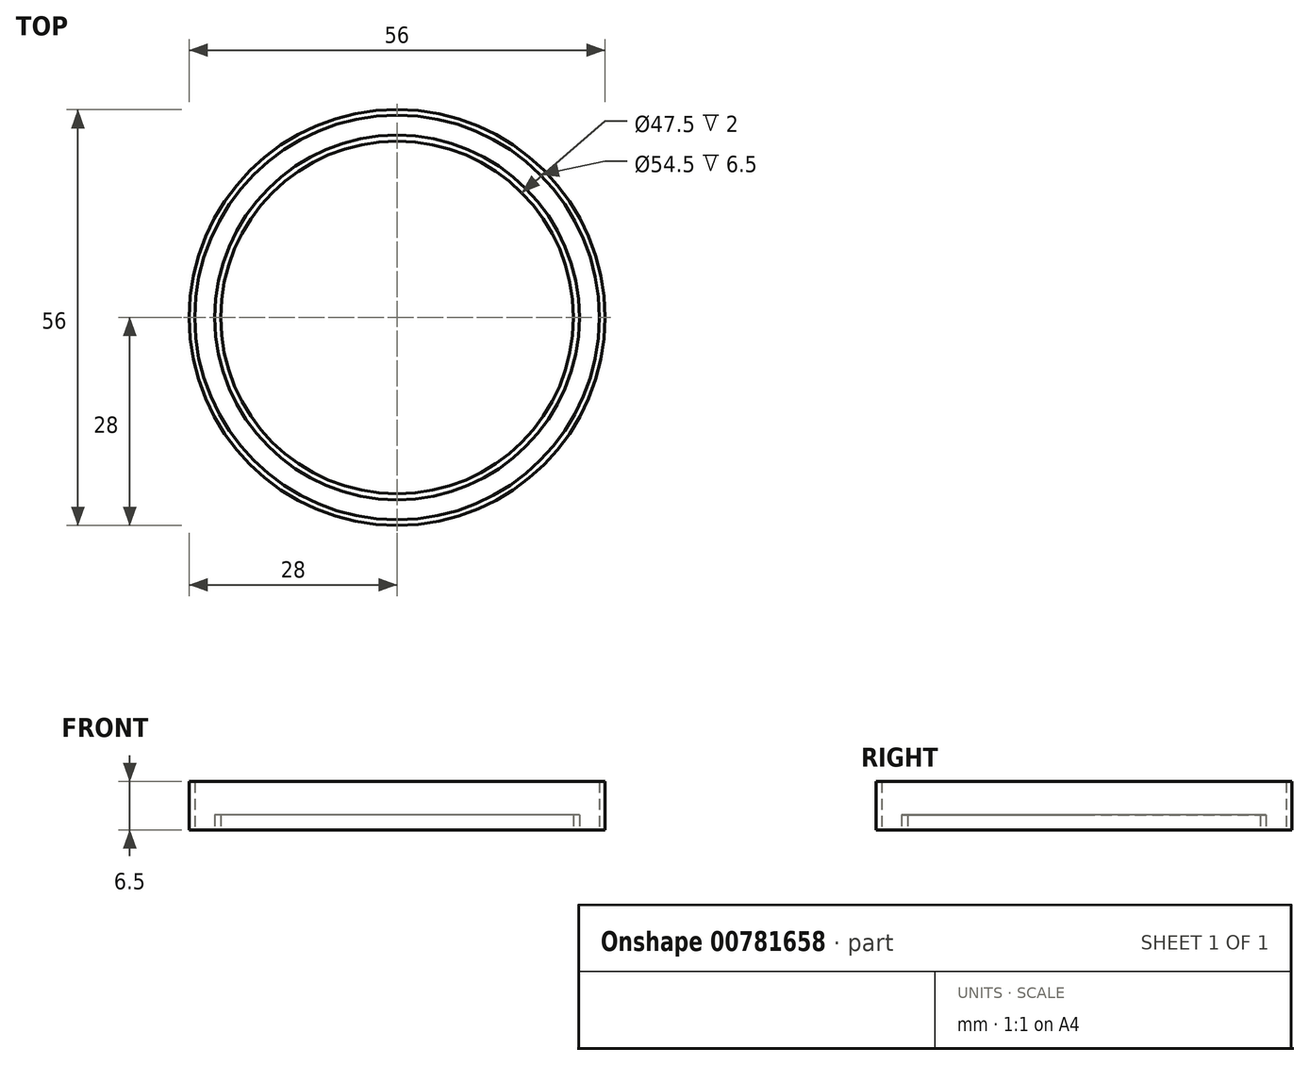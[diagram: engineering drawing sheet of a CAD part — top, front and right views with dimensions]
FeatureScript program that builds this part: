
annotation { "Feature Type Name" : "Feature", "Feature Type Description" : "" }
export const myFeature = defineFeature(function(context is Context, id is Id, definition is map)
    precondition{}
    {
        {
            var Q0;
            Q0=qCreatedBy(makeId("Top.planeOp"),FACE);
            var sketch = newSketch(context, id + "F0", { "sketchPlane" : qUnion([Q0])});
            skCircle(sketch, "E0", {"center": v(0, 0) * mm, "radius": 28 * mm});
            skCircle(sketch, "E1", {"center": v(0, 0) * mm, "radius": 23.75 * mm});
            skCircle(sketch, "E2", {"center": v(0, 0) * mm, "radius": 27.25 * mm});
            skCircle(sketch, "E3", {"center": v(0, 0) * mm, "radius": 24.55 * mm});
            skLineSegment(sketch, "E4", {"start": v(-12.3, -3.3) * mm, "end": v(12.3, -3.3) * mm});
            skLineSegment(sketch, "E5", {"start": v(12.3, -3.3) * mm, "end": v(12.3, -16.25) * mm});
            skLineSegment(sketch, "E6", {"start": v(9.3, -19.25) * mm, "end": v(-9.3, -19.25) * mm});
            skLineSegment(sketch, "E7", {"start": v(-12.3, -3.3) * mm, "end": v(-12.3, -16.25) * mm});
            skPoint(sketch, "E8.visualSharp", {"position": v(-12.3, -19.25) * mm});
            skArc(sketch, "E8.filletArc", {"start": v(-12.3, -16.25) * mm, "mid": v(-11.42, -18.37) * mm, "end": v(-9.3, -19.25) * mm});
            skPoint(sketch, "E9.visualSharp", {"position": v(12.3, -19.25) * mm});
            skArc(sketch, "E9.filletArc", {"start": v(9.3, -19.25) * mm, "mid": v(11.42, -18.37) * mm, "end": v(12.3, -16.25) * mm});
            skSolve(sketch);
        }
        {
            var Q0;
            Q0 = qSketchRegion(id + "F0", true);
            extrude(context, id + "F1", {"entities" : qUnion([Q0]), "depth" : 6.5 * mm, "offsetDistance" : 25 * mm});
        }
        {
            var Q0;
            Q0=makeQuery(id+"F0.imprint","IMPRINT",FACE,{"disambiguationData":[TD([[makeQuery(id+"F0.imprint","IMPRINT",EDGE,{"derivedFrom":sQuery(id+"F0.wireOp",EDGE,"E1")}),-1.0]])]});
            extrude(context, id + "F2", {"entities" : qUnion([Q0]), "depth" : 2 * mm, "offsetDistance" : 25 * mm});
        }
    });
